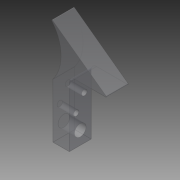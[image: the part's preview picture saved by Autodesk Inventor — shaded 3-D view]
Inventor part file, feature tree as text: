
AUTODESK INVENTOR PART (.ipt)
format: ipt  version: 2014 SP1 (Build 180222100, 222)  size: 114,688 bytes
history: native  units: in
note: dims shown in document units (in); Inventor stores cm internally (conversion verified against a paired STEP export)
features: fillet x4, extrude x2, sketch x2
ambient origin geometry x8: Origin, YZ Plane, XZ Plane, XY Plane, X Axis, Y Axis, Z Axis, Center Point
bodies: Solid1 (feature_tree)
feature tree (8):
  extrude  "Extrusion1"  Depth=1.5in
  extrude  "Extrusion2"  Depth=0.0125in
  fillet  "Fillet1"  Radius=0.125in
  fillet  "Fillet2"  Radius=0.1875in
  fillet  "Fillet3"  Radius=0.5in
  fillet  "Fillet4"  Radius=0.266in
  sketch  "Sketch1"  dims[d0=0.375in d1=1.5in]
  sketch  "Sketch2"  dims[d2=0.875in d3=2.5in d4=0.125in d5=0.1875in d6=0.5in d7=0.0in d8=0.266in d10=0.25in d11=0.3in d12=0.125in d13=0.125in d15=0.1875in d16=0.1562in d17=1.0in d18=0.5in d19=0.0in d20=0.125in d21=0.0125in d22=0.0125in d23=0.0125in d24=0.3125in]
